# Revit family: QF_ZANUSSI_218683_ZCOG102K2G0
name_source: partatom
category: Specialty Equipment
revit_build: Autodesk Revit 2018 (Build: 20190510_1515(x64)
units: mm (PartAtom-declared; Revit-internal decimal feet)

## family parameters
Always vertical = Yes
Cut with Voids When Loaded = No
Part Type = Normal
Room Calculation Point = No
Round Connector Dimension = Use Diameter
Shared = No
Work Plane-Based = No

## types (1)
- QF_ZANUSSI_218683_ZCOG102K2G0
    Accessory = Yes
    Cold Water Size = 19 mm
    Compressed Air Pressure = 0.0 Pa
    Compressed Air Size = 0 mm
    Compressed Air Volume = 0.0 L/s
    Condensate Return Size = 0 mm
    Cycle = 50 Hz
    Depth Actual = 1046 mm  [stored 3.43176 ft]
    Description = MAGISTAR COMBI TI OVEN 10 GN 2/1 - GAS
    Gas Input Pressure = 0
    Gas KW = 47
    Gas Size = 13 mm
    HP = 2 HP
    Height Actual = 1058 mm  [stored 3.47113 ft]
    Hot Water Size = 0 mm
    Item Number = 218683
    Length Actual = 1090 mm  [stored 3.57612 ft]
    Manufacturer = Zanussi
    Model = ZCOG102K2G0
    Phase = 1
    Refrigerant Compressor Remote = Yes
    Refrigeration Liquid Line Size = 0 mm
    Refrigeration Suction Line Size = 0 mm
    Steam Pounds per Hour = 0
    Steam Supply Maximum Pressure = 0.0 Pa
    Steam Supply Minimum Pressure = 0.0 Pa
    Steam Supply Size = 0 mm
    URL = http://www.zanussiprofessional.com
    URL Manufacturer = http://www.zanussiprofessional.com
    Volts = 220 V
    Watts = 139 W
    Weight = 0.00 kg

note: source unit labels omitted for Gas Input Pressure — the stored unit's dimension contradicts the parameter name (converter mislabeling)

note: [stored X ft] marks values corroborated as IEEE doubles in the binary element streams (Revit-internal decimal feet)

## geometry (parser evidence)
native form markers: Blend x17
no freeform markers — native parametric forms only
